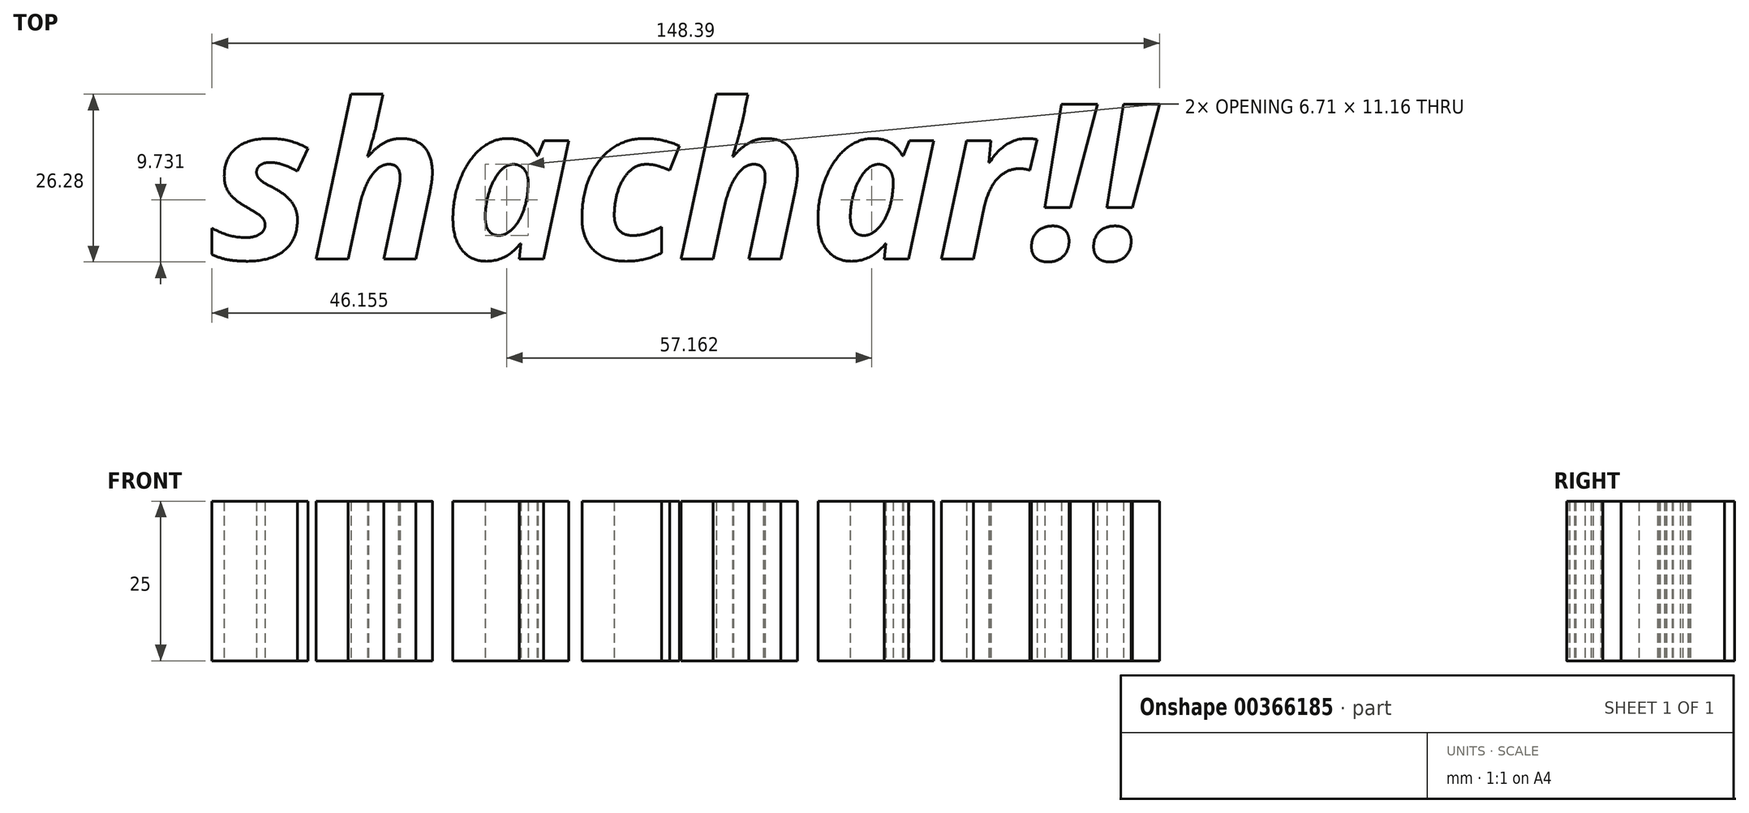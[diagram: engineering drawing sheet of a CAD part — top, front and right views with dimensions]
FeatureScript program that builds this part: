
annotation { "Feature Type Name" : "Feature", "Feature Type Description" : "" }
export const myFeature = defineFeature(function(context is Context, id is Id, definition is map)
    precondition{}
    {
        {
            var Q0;
            Q0=qCreatedBy(makeId("Top.planeOp"),FACE);
            var sketch = newSketch(context, id + "F0", { "sketchPlane" : qUnion([Q0])});
            skText(sketch, "E0", { "text": "shachar!!", "fontName": "OpenSans-BoldItalic.ttf"});
            const initialGuessF0  = {"E0": [-0.07488, -0.01054, 1, 0, 0.02448]};
            skSetInitialGuess(sketch, initialGuessF0);
            skSolve(sketch);
        }
        {
            var Q0;
            Q0 = qSketchRegion(id + "F0", true);
            extrude(context, id + "F1", {"entities" : qUnion([Q0]), "depth" : 25 * mm});
        }
    });
